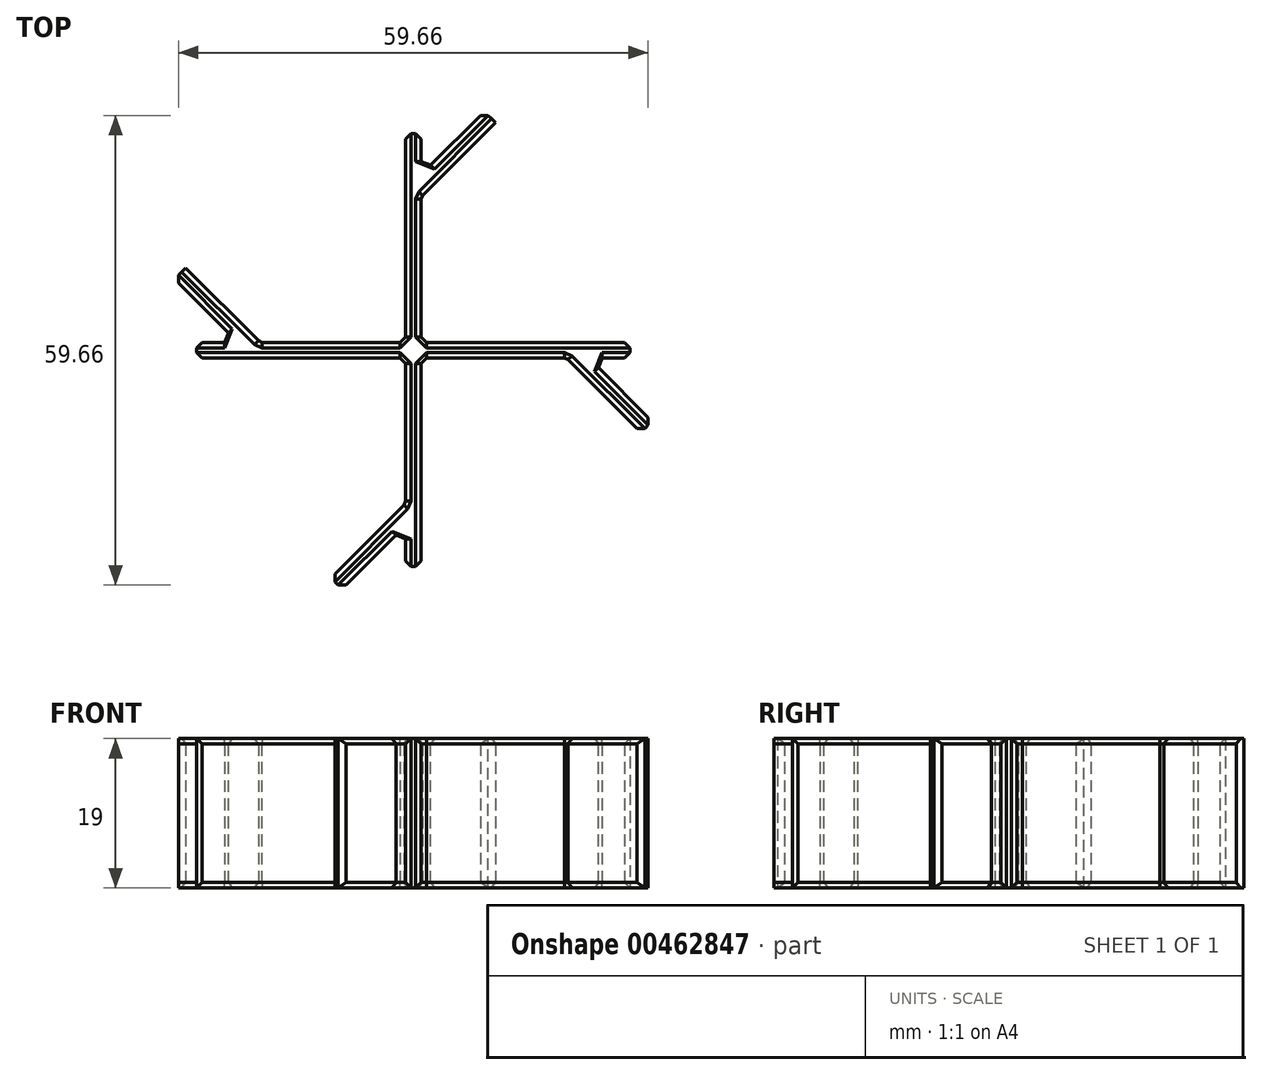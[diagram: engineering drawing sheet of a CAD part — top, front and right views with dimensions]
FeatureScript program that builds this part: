
annotation { "Feature Type Name" : "Feature", "Feature Type Description" : "" }
export const myFeature = defineFeature(function(context is Context, id is Id, definition is map)
    precondition{}
    {
        {
            var Q0;
            Q0=qCreatedBy(makeId("Top.planeOp"),FACE);
            var sketch = newSketch(context, id + "F0", { "sketchPlane" : qUnion([Q0])});
            skLineSegment(sketch, "E0.bottom", {"start": v(0, 0) * mm, "end": v(-2, 0) * mm});
            skLineSegment(sketch, "E0.top", {"start": v(0, 55) * mm, "end": v(-2, 55) * mm});
            skLineSegment(sketch, "E0.left", {"start": v(0, 0) * mm, "end": v(0, 55) * mm});
            skLineSegment(sketch, "E0.right", {"start": v(-2, 0) * mm, "end": v(-2, 55) * mm});
            skLineSegment(sketch, "E1", {"start": v(0, 0) * mm, "end": v(13.96, 0) * mm});
            skLineSegment(sketch, "E2", {"start": v(18.5, 0) * mm, "end": v(26.01, 0) * mm});
            skSolve(sketch);
        }
        {
            var Q0;
            Q0=makeQuery(id+"F0.imprint","IMPRINT",FACE,{"disambiguationData":[TD([[makeQuery(id+"F0.imprint","IMPRINT",EDGE,{"derivedFrom":sQuery(id+"F0.wireOp",EDGE,"E0.bottom")}),-1.0]])]});
            extrude(context, id + "F1", {"entities" : qUnion([Q0]), "depth" : 19 * mm});
        }
        {
            var Q0;
            Q0=qCreatedBy(makeId("Top.planeOp"),FACE);
            var sketch = newSketch(context, id + "F2", { "sketchPlane" : qUnion([Q0])});
            skLineSegment(sketch, "E3", {"start": v(13.67, 0) * mm, "end": v(36.23, 0) * mm});
            skSolve(sketch);
        }
        {
            var Q0;
            Q0=makeQuery(id+"F1.opExtrude","SWEPT_BODY",BODY,{"disambiguationData":[OSD([sQuery(id+"F0.wireOp",EDGE,"E0.bottom"),sQuery(id+"F0.wireOp",EDGE,"E0.top"),sQuery(id+"F0.wireOp",EDGE,"E0.left"),sQuery(id+"F0.wireOp",EDGE,"E0.right")])]});
            var Q1;
            Q1=sQuery(id+"F2.wireOp",EDGE,"E3");
            transform(context, id + "F3", {"entities" : qUnion([Q0]), "transformType" : TransformType.TRANSLATION_DISTANCE, "transformDirection" : qUnion([Q1]), "distance" : 1 * mm, "makeCopy" : false});
        }
        {
            var Q0;
            Q0=qCreatedBy(makeId("Top.planeOp"),FACE);
            var sketch = newSketch(context, id + "F4", { "sketchPlane" : qUnion([Q0])});
            skLineSegment(sketch, "E4", {"start": v(0, 62.06) * mm, "end": v(0, 72.35) * mm});
            skSolve(sketch);
        }
        {
            var Q0;
            Q0=makeQuery(id+"F1.opExtrude","SWEPT_BODY",BODY,{"disambiguationData":[OSD([sQuery(id+"F0.wireOp",EDGE,"E0.bottom"),sQuery(id+"F0.wireOp",EDGE,"E0.top"),sQuery(id+"F0.wireOp",EDGE,"E0.left"),sQuery(id+"F0.wireOp",EDGE,"E0.right")])]});
            var Q1;
            Q1=sQuery(id+"F4.wireOp",EDGE,"E4");
            transform(context, id + "F5", {"entities" : qUnion([Q0]), "transformType" : TransformType.TRANSLATION_DISTANCE, "transformDirection" : qUnion([Q1]), "distance" : 27.5 * mm, "oppositeDirection" : true, "makeCopy" : false});
        }
        {
            var Q0;
            Q0=qCreatedBy(makeId("Front.planeOp"),FACE);
            var sketch = newSketch(context, id + "F6", { "sketchPlane" : qUnion([Q0])});
            skLineSegment(sketch, "E5", {"start": v(0, 0) * mm, "end": v(0, 29.92) * mm});
            skSolve(sketch);
        }
        {
            var Q0;
            Q0=qSketchRegion(id+"F0",true);
            var sketch = newSketch(context, id + "F7", { "sketchPlane" : qUnion([Q0])});
            skLineSegment(sketch, "E6.bottom", {"start": v(5.46, 13.22) * mm, "end": v(7.46, 13.22) * mm});
            skLineSegment(sketch, "E6.top", {"start": v(5.46, 27.22) * mm, "end": v(7.46, 27.22) * mm});
            skLineSegment(sketch, "E6.left", {"start": v(5.46, 13.22) * mm, "end": v(5.46, 27.22) * mm});
            skLineSegment(sketch, "E6.right", {"start": v(7.46, 13.22) * mm, "end": v(7.46, 27.22) * mm});
            skSolve(sketch);
        }
        {
            var Q0;
            Q0=makeQuery(id+"F7.imprint","IMPRINT",FACE,{"disambiguationData":[TD([[makeQuery(id+"F7.imprint","IMPRINT",EDGE,{"derivedFrom":sQuery(id+"F7.wireOp",EDGE,"E6.bottom")}),1.0]])]});
            var Q1;
            Q1=makeQuery(id+"F1.opExtrude","CAP_FACE",FACE,{"disambiguationData":[OSD([sQuery(id+"F0.wireOp",EDGE,"E0.bottom"),sQuery(id+"F0.wireOp",EDGE,"E0.top"),sQuery(id+"F0.wireOp",EDGE,"E0.left"),sQuery(id+"F0.wireOp",EDGE,"E0.right")])],"isStart":false});
            extrude(context, id + "F8", {"entities" : qUnion([Q0]), "endBound" : BoundingType.UP_TO_SURFACE, "endBoundEntityFace" : qUnion([Q1]), "depth" : 25 * mm});
        }
        {
            var Q0;
            Q0=makeQuery(id+"F8.opExtrude","SWEPT_BODY",BODY,{"disambiguationData":[OSD([sQuery(id+"F7.wireOp",EDGE,"E6.bottom"),sQuery(id+"F7.wireOp",EDGE,"E6.top"),sQuery(id+"F7.wireOp",EDGE,"E6.left"),sQuery(id+"F7.wireOp",EDGE,"E6.right")])]});
            var Q1;
            Q1=sQuery(id+"F6.wireOp",EDGE,"E5");
            transform(context, id + "F9", {"entities" : qUnion([Q0]), "transformType" : TransformType.ROTATION, "transformAxis" : qUnion([Q1]), "angle" : 45 * degree, "oppositeDirection" : true, "makeCopy" : false});
        }
        {
            var Q0;
            Q0=makeQuery(id+"F8.opExtrude","SWEPT_FACE",FACE,{"disambiguationData":[OSD([sQuery(id+"F7.wireOp",EDGE,"E6.right")])]});
            var sketch = newSketch(context, id + "F10", { "sketchPlane" : qUnion([Q0])});
            skPoint(sketch, "E7", {"position": v(13.22, 0) * mm});
            skSolve(sketch);
        }
        {
            var Q0;
            Q0=makeQuery(id+"F1.opExtrude","SWEPT_FACE",FACE,{"disambiguationData":[OSD([sQuery(id+"F0.wireOp",EDGE,"E0.left")])]});
            var sketch = newSketch(context, id + "F11", { "sketchPlane" : qUnion([Q0])});
            skPoint(sketch, "E8", {"position": v(18.53, 0) * mm});
            skSolve(sketch);
        }
        {
            var Q0;
            Q0=makeQuery(id+"F8.opExtrude","SWEPT_BODY",BODY,{"disambiguationData":[OSD([sQuery(id+"F7.wireOp",EDGE,"E6.bottom"),sQuery(id+"F7.wireOp",EDGE,"E6.top"),sQuery(id+"F7.wireOp",EDGE,"E6.left"),sQuery(id+"F7.wireOp",EDGE,"E6.right")])]});
            var Q1;
            Q1=sQuery(id+"F11.wireOp",VERTEX,"E8");
            var Q2;
            Q2=sQuery(id+"F10.wireOp",VERTEX,"E7");
            transform(context, id + "F12", {"entities" : qUnion([Q0]), "transformType" : TransformType.TRANSLATION_DISTANCE, "transformDirection" : qUnion([Q1, Q2]), "distance" : 20.53 * mm, "oppositeDirection" : true, "makeCopy" : false});
        }
        {
            var Q0;
            Q0=qCreatedBy(makeId("Front.planeOp"),FACE);
            var sketch = newSketch(context, id + "F13", { "sketchPlane" : qUnion([Q0])});
            skLineSegment(sketch, "E9", {"start": v(0, 0) * mm, "end": v(0, 44.04) * mm});
            skSolve(sketch);
        }
        {
            var Q0;
            Q0=makeQuery(id+"F1.opExtrude","SWEPT_BODY",BODY,{"disambiguationData":[OSD([sQuery(id+"F0.wireOp",EDGE,"E0.bottom"),sQuery(id+"F0.wireOp",EDGE,"E0.top"),sQuery(id+"F0.wireOp",EDGE,"E0.left"),sQuery(id+"F0.wireOp",EDGE,"E0.right")])]});
            var Q1;
            Q1=makeQuery(id+"F8.opExtrude","SWEPT_BODY",BODY,{"disambiguationData":[OSD([sQuery(id+"F7.wireOp",EDGE,"E6.bottom"),sQuery(id+"F7.wireOp",EDGE,"E6.top"),sQuery(id+"F7.wireOp",EDGE,"E6.left"),sQuery(id+"F7.wireOp",EDGE,"E6.right")])]});
            var Q2;
            Q2=sQuery(id+"F13.wireOp",EDGE,"E9");
            circularPattern(context, id + "F14", {"entities" : qUnion([Q0, Q1]), "axis" : qUnion([Q2]), "angle" : 360 * degree, "instanceCount" : 4, "equalSpace" : true});
        }
        {
            var Q0;
            Q0=makeQuery(id+"F1.opExtrude","SWEPT_BODY",BODY,{"disambiguationData":[OSD([sQuery(id+"F0.wireOp",EDGE,"E0.bottom"),sQuery(id+"F0.wireOp",EDGE,"E0.top"),sQuery(id+"F0.wireOp",EDGE,"E0.left"),sQuery(id+"F0.wireOp",EDGE,"E0.right")])]});
            var Q1;
            Q1=makeQuery(id+"F8.opExtrude","SWEPT_BODY",BODY,{"disambiguationData":[OSD([sQuery(id+"F7.wireOp",EDGE,"E6.bottom"),sQuery(id+"F7.wireOp",EDGE,"E6.top"),sQuery(id+"F7.wireOp",EDGE,"E6.left"),sQuery(id+"F7.wireOp",EDGE,"E6.right")])]});
            var Q2;
            Q2=makeQuery(id+"F14.opPattern","COPY",BODY,{"derivedFrom":makeQuery(id+"F1.opExtrude","SWEPT_BODY",BODY,{"disambiguationData":[OSD([sQuery(id+"F0.wireOp",EDGE,"E0.bottom"),sQuery(id+"F0.wireOp",EDGE,"E0.top"),sQuery(id+"F0.wireOp",EDGE,"E0.left"),sQuery(id+"F0.wireOp",EDGE,"E0.right")])]}),"instanceName":"1"});
            var Q3;
            Q3=makeQuery(id+"F14.opPattern","COPY",BODY,{"derivedFrom":makeQuery(id+"F8.opExtrude","SWEPT_BODY",BODY,{"disambiguationData":[OSD([sQuery(id+"F7.wireOp",EDGE,"E6.bottom"),sQuery(id+"F7.wireOp",EDGE,"E6.top"),sQuery(id+"F7.wireOp",EDGE,"E6.left"),sQuery(id+"F7.wireOp",EDGE,"E6.right")])]}),"instanceName":"1"});
            var Q4;
            Q4=makeQuery(id+"F14.opPattern","COPY",BODY,{"derivedFrom":makeQuery(id+"F1.opExtrude","SWEPT_BODY",BODY,{"disambiguationData":[OSD([sQuery(id+"F0.wireOp",EDGE,"E0.bottom"),sQuery(id+"F0.wireOp",EDGE,"E0.top"),sQuery(id+"F0.wireOp",EDGE,"E0.left"),sQuery(id+"F0.wireOp",EDGE,"E0.right")])]}),"instanceName":"2"});
            var Q5;
            Q5=makeQuery(id+"F14.opPattern","COPY",BODY,{"derivedFrom":makeQuery(id+"F8.opExtrude","SWEPT_BODY",BODY,{"disambiguationData":[OSD([sQuery(id+"F7.wireOp",EDGE,"E6.bottom"),sQuery(id+"F7.wireOp",EDGE,"E6.top"),sQuery(id+"F7.wireOp",EDGE,"E6.left"),sQuery(id+"F7.wireOp",EDGE,"E6.right")])]}),"instanceName":"2"});
            var Q6;
            Q6=makeQuery(id+"F14.opPattern","COPY",BODY,{"derivedFrom":makeQuery(id+"F1.opExtrude","SWEPT_BODY",BODY,{"disambiguationData":[OSD([sQuery(id+"F0.wireOp",EDGE,"E0.bottom"),sQuery(id+"F0.wireOp",EDGE,"E0.top"),sQuery(id+"F0.wireOp",EDGE,"E0.left"),sQuery(id+"F0.wireOp",EDGE,"E0.right")])]}),"instanceName":"3"});
            var Q7;
            Q7=makeQuery(id+"F14.opPattern","COPY",BODY,{"derivedFrom":makeQuery(id+"F8.opExtrude","SWEPT_BODY",BODY,{"disambiguationData":[OSD([sQuery(id+"F7.wireOp",EDGE,"E6.bottom"),sQuery(id+"F7.wireOp",EDGE,"E6.top"),sQuery(id+"F7.wireOp",EDGE,"E6.left"),sQuery(id+"F7.wireOp",EDGE,"E6.right")])]}),"instanceName":"3"});
            booleanBodies(context, id + "F15", {"operationType" : BooleanOperationType.UNION, "tools" : qUnion([Q0, Q1, Q2, Q3, Q4, Q5, Q6, Q7])});
        }
        {
            var Q0;
            {var subQ1=sQuery(id+"F0.wireOp",EDGE,"E0.right");var subQ8=makeQuery(id+"F1.opExtrude","SWEPT_FACE",FACE,{"disambiguationData":[OSD([subQ1])]});Q0=makeQuery(id+"F15.opBoolean","SPLIT",FACE,{"disambiguationData":[TD([subQ8])],"derivedFrom":makeQuery(id+"F14.opPattern","COPY",FACE,{"derivedFrom":subQ8,"instanceName":"1"})});}
            var Q1;
            {var subQ2=sQuery(id+"F0.wireOp",EDGE,"E0.left");var subQ4=sQuery(id+"F0.wireOp",EDGE,"E0.bottom");Q1=makeQuery(id+"F15.opBoolean","SPLIT",FACE,{"disambiguationData":[TD([makeQuery(id+"F1.opExtrude","SWEPT_FACE",FACE,{"disambiguationData":[OSD([subQ4])]})])],"derivedFrom":makeQuery(id+"F1.opExtrude","SWEPT_FACE",FACE,{"disambiguationData":[OSD([subQ2])]})});}
            var Q2;
            Q2=makeQuery(id+"F14.opPattern","COPY",FACE,{"derivedFrom":makeQuery(id+"F8.opExtrude","SWEPT_FACE",FACE,{"disambiguationData":[OSD([sQuery(id+"F7.wireOp",EDGE,"E6.left")])]}),"instanceName":"2"});
            var Q3;
            {var subQ0=sQuery(id+"F7.wireOp",EDGE,"E6.right");var subQ3=sQuery(id+"F0.wireOp",EDGE,"E0.left");var subQ9=makeQuery(id+"F1.opExtrude","SWEPT_FACE",FACE,{"disambiguationData":[OSD([subQ3])]});Q3=makeQuery(id+"F15.opBoolean","SPLIT",FACE,{"disambiguationData":[TD([makeQuery(id+"F8.opExtrude","SWEPT_FACE",FACE,{"disambiguationData":[OSD([subQ0])]})])],"derivedFrom":subQ9});}
            var Q4;
            Q4=makeQuery(id+"F14.opPattern","COPY",FACE,{"derivedFrom":makeQuery(id+"F8.opExtrude","SWEPT_FACE",FACE,{"disambiguationData":[OSD([sQuery(id+"F7.wireOp",EDGE,"E6.left")])]}),"instanceName":"3"});
            var Q5;
            {var subQ2=sQuery(id+"F0.wireOp",EDGE,"E0.right");var subQ5=sQuery(id+"F0.wireOp",EDGE,"E0.bottom");Q5=makeQuery(id+"F15.opBoolean","SPLIT",FACE,{"disambiguationData":[TD([makeQuery(id+"F14.opPattern","COPY",FACE,{"derivedFrom":makeQuery(id+"F1.opExtrude","SWEPT_FACE",FACE,{"disambiguationData":[OSD([subQ5])]}),"instanceName":"1"})])],"derivedFrom":makeQuery(id+"F14.opPattern","COPY",FACE,{"derivedFrom":makeQuery(id+"F1.opExtrude","SWEPT_FACE",FACE,{"disambiguationData":[OSD([subQ2])]}),"instanceName":"1"})});}
            var Q6;
            {var subQ2=sQuery(id+"F0.wireOp",EDGE,"E0.left");var subQ8=makeQuery(id+"F1.opExtrude","SWEPT_FACE",FACE,{"disambiguationData":[OSD([subQ2])]});Q6=makeQuery(id+"F15.opBoolean","SPLIT",FACE,{"disambiguationData":[TD([subQ8])],"derivedFrom":makeQuery(id+"F14.opPattern","COPY",FACE,{"derivedFrom":subQ8,"instanceName":"1"})});}
            var Q7;
            {var subQ3=sQuery(id+"F0.wireOp",EDGE,"E0.left");var subQ4=sQuery(id+"F0.wireOp",EDGE,"E0.top");Q7=makeQuery(id+"F15.opBoolean","SPLIT",FACE,{"disambiguationData":[TD([makeQuery(id+"F1.opExtrude","SWEPT_FACE",FACE,{"disambiguationData":[OSD([subQ4])]})])],"derivedFrom":makeQuery(id+"F1.opExtrude","SWEPT_FACE",FACE,{"disambiguationData":[OSD([subQ3])]})});}
            var Q8;
            Q8=makeQuery(id+"F8.opExtrude","SWEPT_EDGE",EDGE,{"disambiguationData":[OSD([sQuery(id+"F7.wireOp",EDGE,"E6.top"),sQuery(id+"F7.wireOp",EDGE,"E6.left")])]});
            var Q9;
            Q9=makeQuery(id+"F8.opExtrude","SWEPT_FACE",FACE,{"disambiguationData":[OSD([sQuery(id+"F7.wireOp",EDGE,"E6.left")])]});
            var Q10;
            {var subQ1=sQuery(id+"F0.wireOp",EDGE,"E0.right");var subQ3=sQuery(id+"F0.wireOp",EDGE,"E0.top");Q10=makeQuery(id+"F15.opBoolean","SPLIT",FACE,{"disambiguationData":[TD([makeQuery(id+"F1.opExtrude","SWEPT_FACE",FACE,{"disambiguationData":[OSD([subQ3])]})])],"derivedFrom":makeQuery(id+"F1.opExtrude","SWEPT_FACE",FACE,{"disambiguationData":[OSD([subQ1])]})});}
            var Q11;
            {var subQ2=sQuery(id+"F0.wireOp",EDGE,"E0.right");var subQ3=sQuery(id+"F0.wireOp",EDGE,"E0.left");Q11=makeQuery(id+"F15.opBoolean","SPLIT",FACE,{"disambiguationData":[TD([makeQuery(id+"F1.opExtrude","SWEPT_FACE",FACE,{"disambiguationData":[OSD([subQ2])]})])],"derivedFrom":makeQuery(id+"F14.opPattern","COPY",FACE,{"derivedFrom":makeQuery(id+"F1.opExtrude","SWEPT_FACE",FACE,{"disambiguationData":[OSD([subQ3])]}),"instanceName":"1"})});}
            var Q12;
            Q12=makeQuery(id+"F14.opPattern","COPY",FACE,{"derivedFrom":makeQuery(id+"F8.opExtrude","SWEPT_FACE",FACE,{"disambiguationData":[OSD([sQuery(id+"F7.wireOp",EDGE,"E6.left")])]}),"instanceName":"1"});
            var Q13;
            {var subQ3=sQuery(id+"F0.wireOp",EDGE,"E0.left");var subQ4=sQuery(id+"F0.wireOp",EDGE,"E0.top");Q13=makeQuery(id+"F15.opBoolean","SPLIT",FACE,{"disambiguationData":[TD([makeQuery(id+"F14.opPattern","COPY",FACE,{"derivedFrom":makeQuery(id+"F1.opExtrude","SWEPT_FACE",FACE,{"disambiguationData":[OSD([subQ4])]}),"instanceName":"1"})])],"derivedFrom":makeQuery(id+"F14.opPattern","COPY",FACE,{"derivedFrom":makeQuery(id+"F1.opExtrude","SWEPT_FACE",FACE,{"disambiguationData":[OSD([subQ3])]}),"instanceName":"1"})});}
            var Q14;
            Q14=makeQuery(id+"F14.opPattern","COPY",FACE,{"derivedFrom":makeQuery(id+"F8.opExtrude","SWEPT_FACE",FACE,{"disambiguationData":[OSD([sQuery(id+"F7.wireOp",EDGE,"E6.right")])]}),"instanceName":"2"});
            var Q15;
            {var subQ2=sQuery(id+"F0.wireOp",EDGE,"E0.right");var subQ5=sQuery(id+"F0.wireOp",EDGE,"E0.bottom");Q15=makeQuery(id+"F15.opBoolean","SPLIT",FACE,{"disambiguationData":[TD([makeQuery(id+"F1.opExtrude","SWEPT_FACE",FACE,{"disambiguationData":[OSD([subQ5])]})])],"derivedFrom":makeQuery(id+"F1.opExtrude","SWEPT_FACE",FACE,{"disambiguationData":[OSD([subQ2])]})});}
            var Q16;
            Q16=makeQuery(id+"F14.opPattern","COPY",FACE,{"derivedFrom":makeQuery(id+"F8.opExtrude","SWEPT_FACE",FACE,{"disambiguationData":[OSD([sQuery(id+"F7.wireOp",EDGE,"E6.right")])]}),"instanceName":"3"});
            chamfer(context, id + "F16", {"entities" : qUnion([Q0, Q1, Q2, Q3, Q4, Q5, Q6, Q7, Q8, Q9, Q10, Q11, Q12, Q13, Q14, Q15, Q16]), "width" : 0.7 * mm, "tangentPropagation" : true});
        }
    });
